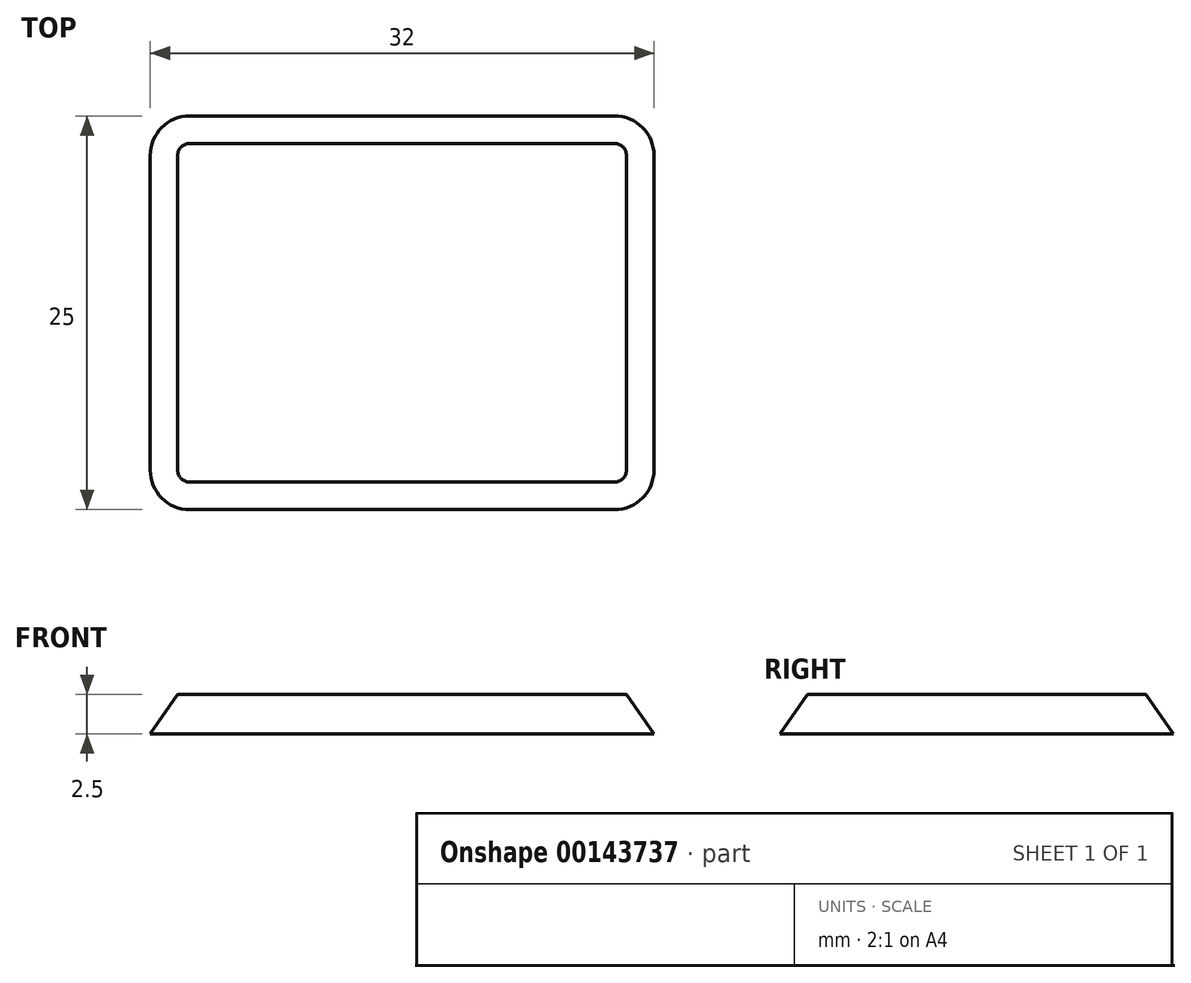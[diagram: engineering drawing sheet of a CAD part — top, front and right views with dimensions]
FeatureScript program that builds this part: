
annotation { "Feature Type Name" : "Feature", "Feature Type Description" : "" }
export const myFeature = defineFeature(function(context is Context, id is Id, definition is map)
    precondition{}
    {
        {
            var Q0;
            Q0=qCreatedBy(makeId("Top.planeOp"),FACE);
            var sketch = newSketch(context, id + "F0", { "sketchPlane" : qUnion([Q0])});
            skLineSegment(sketch, "E0.bottom", {"start": v(-16, 12.5) * mm, "end": v(16, 12.5) * mm});
            skLineSegment(sketch, "E0.top", {"start": v(-16, -12.5) * mm, "end": v(16, -12.5) * mm});
            skLineSegment(sketch, "E0.left", {"start": v(-16, 12.5) * mm, "end": v(-16, -12.5) * mm});
            skLineSegment(sketch, "E0.right", {"start": v(16, 12.5) * mm, "end": v(16, -12.5) * mm});
            skPoint(sketch, "E0.middle", {"position": v(0, 0) * mm});
            skSolve(sketch);
        }
        {
            var Q0;
            Q0=makeQuery(id+"F0.imprint","IMPRINT",FACE,{"disambiguationData":[TD([[makeQuery(id+"F0.imprint","IMPRINT",EDGE,{"derivedFrom":sQuery(id+"F0.wireOp",EDGE,"E0.bottom")}),-1.0]])]});
            extrude(context, id + "F1", {"entities" : qUnion([Q0]), "depth" : 2.5 * mm});
        }
        {
            var Q0;
            Q0=makeQuery(id+"F1.opExtrude","SWEPT_EDGE",EDGE,{"disambiguationData":[OSD([sQuery(id+"F0.wireOp",EDGE,"E0.top"),sQuery(id+"F0.wireOp",EDGE,"E0.left")])]});
            var Q1;
            Q1=makeQuery(id+"F1.opExtrude","SWEPT_EDGE",EDGE,{"disambiguationData":[OSD([sQuery(id+"F0.wireOp",EDGE,"E0.top"),sQuery(id+"F0.wireOp",EDGE,"E0.right")])]});
            var Q2;
            Q2=makeQuery(id+"F1.opExtrude","SWEPT_EDGE",EDGE,{"disambiguationData":[OSD([sQuery(id+"F0.wireOp",EDGE,"E0.bottom"),sQuery(id+"F0.wireOp",EDGE,"E0.right")])]});
            var Q3;
            Q3=makeQuery(id+"F1.opExtrude","SWEPT_EDGE",EDGE,{"disambiguationData":[OSD([sQuery(id+"F0.wireOp",EDGE,"E0.bottom"),sQuery(id+"F0.wireOp",EDGE,"E0.left")])]});
            fillet(context, id + "F2", {"entities" : qUnion([Q0, Q1, Q2, Q3]), "radius" : 2.5 * mm, "tangentPropagation" : true, "allowEdgeOverflow" : false});
        }
        {
            var Q0;
            Q0=makeQuery(id+"F1.opExtrude","CAP_EDGE",EDGE,{"disambiguationData":[OSD([sQuery(id+"F0.wireOp",EDGE,"E0.top")])],"isStart":false});
            var Q1;
            Q1=makeQuery(id+"F1.opExtrude","CAP_EDGE",EDGE,{"disambiguationData":[OSD([sQuery(id+"F0.wireOp",EDGE,"E0.left")])],"isStart":false});
            var Q2;
            {var subQ0=sQuery(id+"F0.wireOp",EDGE,"E0.right");var subQ1=sQuery(id+"F0.wireOp",EDGE,"E0.top");Q2=makeQuery(id+"F2.opFillet","BLEND_EDGE",EDGE,{"blendedFrom":[makeQuery(id+"F1.opExtrude","SWEPT_EDGE",EDGE,{"disambiguationData":[OSD([subQ1,subQ0])]}),makeQuery(id+"F1.opExtrude","CAP_FACE",FACE,{"disambiguationData":[OSD([sQuery(id+"F0.wireOp",EDGE,"E0.bottom"),subQ1,sQuery(id+"F0.wireOp",EDGE,"E0.left"),subQ0])],"isStart":false})],"blendedInto":[makeQuery(id+"F1.opExtrude","CAP_FACE",FACE,{"disambiguationData":[OSD([sQuery(id+"F0.wireOp",EDGE,"E0.bottom"),subQ1,sQuery(id+"F0.wireOp",EDGE,"E0.left"),subQ0])],"isStart":false})]});}
            var Q3;
            Q3=makeQuery(id+"F1.opExtrude","CAP_EDGE",EDGE,{"disambiguationData":[OSD([sQuery(id+"F0.wireOp",EDGE,"E0.right")])],"isStart":false});
            var Q4;
            {var subQ0=sQuery(id+"F0.wireOp",EDGE,"E0.right");var subQ1=sQuery(id+"F0.wireOp",EDGE,"E0.bottom");Q4=makeQuery(id+"F2.opFillet","BLEND_EDGE",EDGE,{"blendedFrom":[makeQuery(id+"F1.opExtrude","SWEPT_EDGE",EDGE,{"disambiguationData":[OSD([subQ1,subQ0])]}),makeQuery(id+"F1.opExtrude","CAP_FACE",FACE,{"disambiguationData":[OSD([subQ1,sQuery(id+"F0.wireOp",EDGE,"E0.top"),sQuery(id+"F0.wireOp",EDGE,"E0.left"),subQ0])],"isStart":false})],"blendedInto":[makeQuery(id+"F1.opExtrude","CAP_FACE",FACE,{"disambiguationData":[OSD([subQ1,sQuery(id+"F0.wireOp",EDGE,"E0.top"),sQuery(id+"F0.wireOp",EDGE,"E0.left"),subQ0])],"isStart":false})]});}
            var Q5;
            Q5=makeQuery(id+"F1.opExtrude","CAP_EDGE",EDGE,{"disambiguationData":[OSD([sQuery(id+"F0.wireOp",EDGE,"E0.bottom")])],"isStart":false});
            var Q6;
            {var subQ0=sQuery(id+"F0.wireOp",EDGE,"E0.left");var subQ1=sQuery(id+"F0.wireOp",EDGE,"E0.bottom");Q6=makeQuery(id+"F2.opFillet","BLEND_EDGE",EDGE,{"blendedFrom":[makeQuery(id+"F1.opExtrude","SWEPT_EDGE",EDGE,{"disambiguationData":[OSD([subQ1,subQ0])]}),makeQuery(id+"F1.opExtrude","CAP_FACE",FACE,{"disambiguationData":[OSD([subQ1,sQuery(id+"F0.wireOp",EDGE,"E0.top"),subQ0,sQuery(id+"F0.wireOp",EDGE,"E0.right")])],"isStart":false})],"blendedInto":[makeQuery(id+"F1.opExtrude","CAP_FACE",FACE,{"disambiguationData":[OSD([subQ1,sQuery(id+"F0.wireOp",EDGE,"E0.top"),subQ0,sQuery(id+"F0.wireOp",EDGE,"E0.right")])],"isStart":false})]});}
            var Q7;
            {var subQ0=sQuery(id+"F0.wireOp",EDGE,"E0.left");var subQ1=sQuery(id+"F0.wireOp",EDGE,"E0.top");Q7=makeQuery(id+"F2.opFillet","BLEND_EDGE",EDGE,{"blendedFrom":[makeQuery(id+"F1.opExtrude","SWEPT_EDGE",EDGE,{"disambiguationData":[OSD([subQ1,subQ0])]}),makeQuery(id+"F1.opExtrude","CAP_FACE",FACE,{"disambiguationData":[OSD([sQuery(id+"F0.wireOp",EDGE,"E0.bottom"),subQ1,subQ0,sQuery(id+"F0.wireOp",EDGE,"E0.right")])],"isStart":false})],"blendedInto":[makeQuery(id+"F1.opExtrude","CAP_FACE",FACE,{"disambiguationData":[OSD([sQuery(id+"F0.wireOp",EDGE,"E0.bottom"),subQ1,subQ0,sQuery(id+"F0.wireOp",EDGE,"E0.right")])],"isStart":false})]});}
            chamfer(context, id + "F3", {"entities" : qUnion([Q0, Q1, Q2, Q3, Q4, Q5, Q6, Q7]), "chamferType" : ChamferType.OFFSET_ANGLE, "width" : 2.5 * mm, "oppositeDirection" : true, "angle" : 35 * degree, "tangentPropagation" : true});
        }
    });
